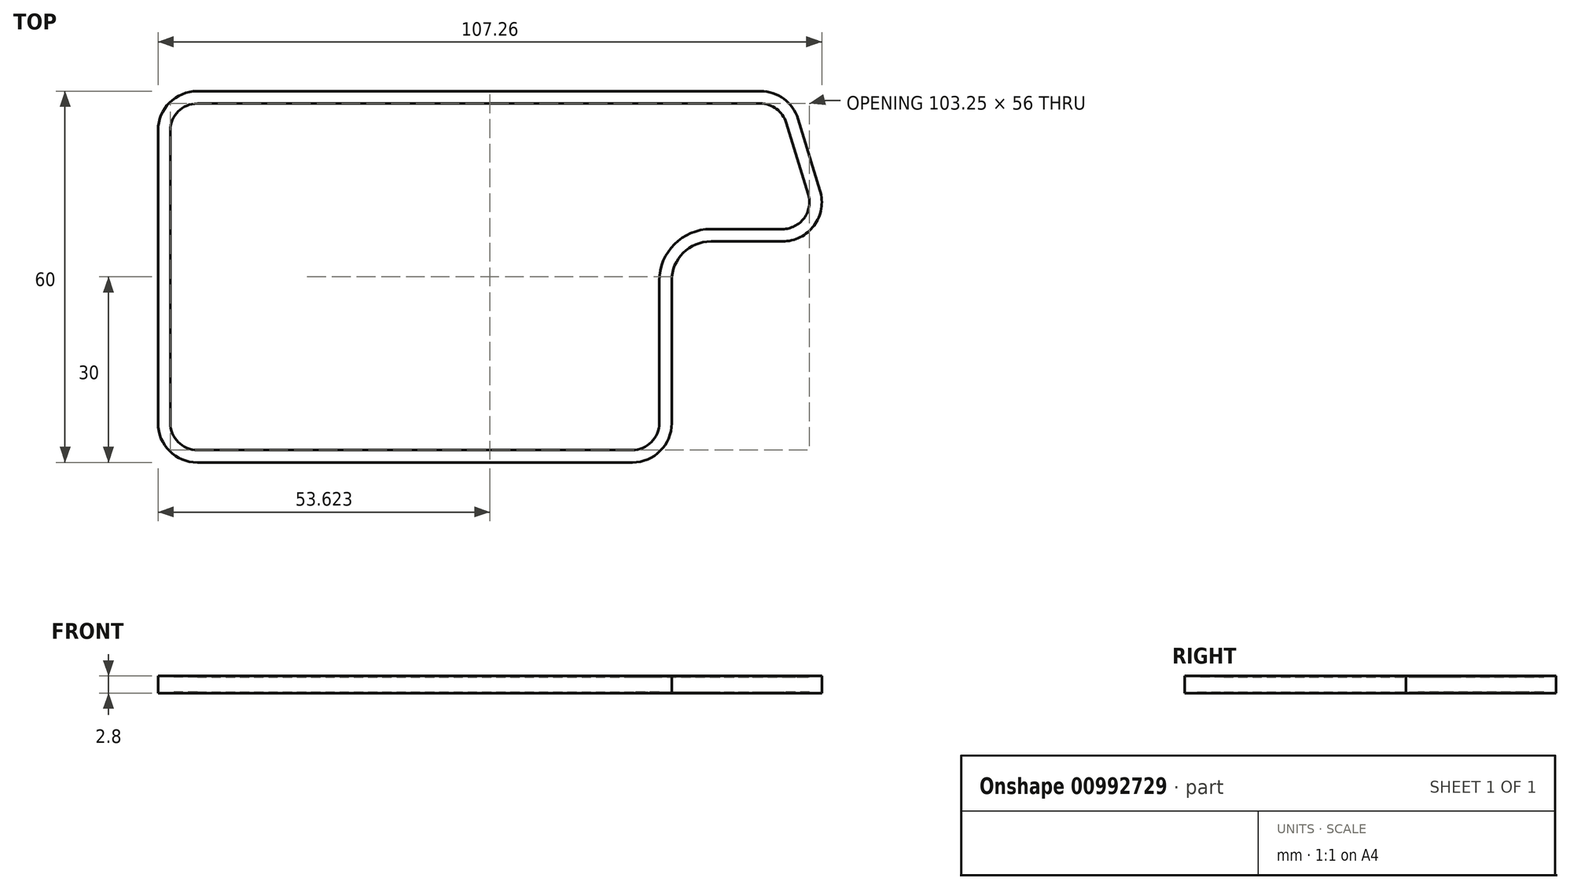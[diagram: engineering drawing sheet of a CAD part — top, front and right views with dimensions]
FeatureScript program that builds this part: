
annotation { "Feature Type Name" : "Feature", "Feature Type Description" : "" }
export const myFeature = defineFeature(function(context is Context, id is Id, definition is map)
    precondition{}
    {
        {
            var Q0;
            Q0=qCreatedBy(makeId("Top.planeOp"),FACE);
            var sketch = newSketch(context, id + "F0", { "sketchPlane" : qUnion([Q0])});
            skLineSegment(sketch, "E0.bottom", {"start": v(-35.15, -30) * mm, "end": v(35.15, -30) * mm});
            skLineSegment(sketch, "E0.top", {"start": v(-35.15, 30) * mm, "end": v(41.5, 30) * mm});
            skLineSegment(sketch, "E0.left", {"start": v(-41.5, -23.65) * mm, "end": v(-41.5, 23.65) * mm});
            skLineSegment(sketch, "E0.right", {"start": v(41.5, -23.65) * mm, "end": v(41.5, -0.64) * mm});
            skPoint(sketch, "E0.middle", {"position": v(0, 0) * mm});
            skPoint(sketch, "E1.visualSharp", {"position": v(-41.5, 30) * mm});
            skArc(sketch, "E1.filletArc", {"start": v(-35.15, 30) * mm, "mid": v(-39.64, 28.14) * mm, "end": v(-41.5, 23.65) * mm});
            skPoint(sketch, "E2.visualSharp", {"position": v(-41.5, -30) * mm});
            skArc(sketch, "E2.filletArc", {"start": v(-41.5, -23.65) * mm, "mid": v(-39.64, -28.14) * mm, "end": v(-35.15, -30) * mm});
            skPoint(sketch, "E3.visualSharp", {"position": v(41.5, -30) * mm});
            skArc(sketch, "E3.filletArc", {"start": v(35.15, -30) * mm, "mid": v(39.64, -28.14) * mm, "end": v(41.5, -23.65) * mm});
            skLineSegment(sketch, "E4.bottom", {"start": v(41.5, 30) * mm, "end": v(55.85, 30) * mm});
            skLineSegment(sketch, "E4.top", {"start": v(47.85, 5.72) * mm, "end": v(59.4, 5.72) * mm});
            skLineSegment(sketch, "E4.right", {"start": v(61.93, 25.51) * mm, "end": v(65.48, 13.93) * mm});
            skPoint(sketch, "E5.visualSharp", {"position": v(60.55, 30) * mm});
            skArc(sketch, "E5.filletArc", {"start": v(61.93, 25.51) * mm, "mid": v(59.63, 28.76) * mm, "end": v(55.85, 30) * mm});
            skPoint(sketch, "E6.visualSharp", {"position": v(68, 5.72) * mm});
            skArc(sketch, "E6.filletArc", {"start": v(59.4, 5.72) * mm, "mid": v(64.51, 8.29) * mm, "end": v(65.48, 13.93) * mm});
            skPoint(sketch, "E7.visualSharp", {"position": v(41.5, 5.72) * mm});
            skArc(sketch, "E7.filletArc", {"start": v(47.85, 5.72) * mm, "mid": v(43.36, 3.86) * mm, "end": v(41.5, -0.64) * mm});
            skSolve(sketch);
        }
        {
            var Q0;
            Q0=makeQuery(id+"F0.imprint","IMPRINT",FACE,{"disambiguationData":[TD([[makeQuery(id+"F0.imprint","IMPRINT",EDGE,{"derivedFrom":sQuery(id+"F0.wireOp",EDGE,"E0.bottom")}),1.0]])]});
            extrude(context, id + "F1", {"entities" : qUnion([Q0]), "depth" : 2.8 * mm, "offsetDistance" : 25.4 * mm});
        }
        {
            var Q0;
            Q0=makeQuery(id+"F1.opExtrude","CAP_FACE",FACE,{"disambiguationData":[OSD([sQuery(id+"F0.wireOp",EDGE,"E0.bottom"),sQuery(id+"F0.wireOp",EDGE,"E0.top"),sQuery(id+"F0.wireOp",EDGE,"E0.left"),sQuery(id+"F0.wireOp",EDGE,"E0.right"),sQuery(id+"F0.wireOp",EDGE,"E1.filletArc"),sQuery(id+"F0.wireOp",EDGE,"E2.filletArc"),sQuery(id+"F0.wireOp",EDGE,"E3.filletArc"),sQuery(id+"F0.wireOp",EDGE,"E4.bottom"),sQuery(id+"F0.wireOp",EDGE,"E4.top"),sQuery(id+"F0.wireOp",EDGE,"E4.right"),sQuery(id+"F0.wireOp",EDGE,"E5.filletArc"),sQuery(id+"F0.wireOp",EDGE,"E6.filletArc"),sQuery(id+"F0.wireOp",EDGE,"E7.filletArc")])],"isStart":false});
            var sketch = newSketch(context, id + "F2", { "sketchPlane" : qUnion([Q0])});
            skLineSegment(sketch, "E8.0", {"start": v(47.85, 7.72) * mm, "end": v(59.4, 7.72) * mm});
            skArc(sketch, "E8.1", {"start": v(-35.15, 28) * mm, "mid": v(-38.23, 26.73) * mm, "end": v(-39.5, 23.65) * mm});
            skLineSegment(sketch, "E8.2", {"start": v(-35.15, 28) * mm, "end": v(55.85, 28) * mm});
            skArc(sketch, "E8.3", {"start": v(60.01, 24.92) * mm, "mid": v(58.44, 27.15) * mm, "end": v(55.85, 28) * mm});
            skLineSegment(sketch, "E8.4", {"start": v(60.01, 24.92) * mm, "end": v(63.56, 13.34) * mm});
            skLineSegment(sketch, "E8.5", {"start": v(-39.5, -23.65) * mm, "end": v(-39.5, 23.65) * mm});
            skArc(sketch, "E8.6", {"start": v(59.4, 7.72) * mm, "mid": v(62.9, 9.48) * mm, "end": v(63.56, 13.34) * mm});
            skArc(sketch, "E8.7", {"start": v(-39.5, -23.65) * mm, "mid": v(-38.23, -26.73) * mm, "end": v(-35.15, -28) * mm});
            skLineSegment(sketch, "E8.8", {"start": v(-35.15, -28) * mm, "end": v(35.15, -28) * mm});
            skArc(sketch, "E8.9", {"start": v(35.15, -28) * mm, "mid": v(38.23, -26.73) * mm, "end": v(39.5, -23.65) * mm});
            skLineSegment(sketch, "E8.10", {"start": v(39.5, -23.65) * mm, "end": v(39.5, -0.63) * mm});
            skArc(sketch, "E8.11", {"start": v(47.85, 7.72) * mm, "mid": v(41.95, 5.27) * mm, "end": v(39.5, -0.63) * mm});
            skSolve(sketch);
        }
        {
            var Q0;
            Q0 = qSketchRegion(id + "F2", true);
            extrude(context, id + "F3", {"entities" : qUnion([Q0]), "operationType" : NewBodyOperationType.REMOVE, "oppositeDirection" : true, "depth" : .2 * mm, "offsetDistance" : 25 * mm});
        }
        {
            var Q0;
            Q0=makeQuery(id+"F1.opExtrude","CAP_FACE",FACE,{"disambiguationData":[OSD([sQuery(id+"F0.wireOp",EDGE,"E0.bottom"),sQuery(id+"F0.wireOp",EDGE,"E0.top"),sQuery(id+"F0.wireOp",EDGE,"E0.left"),sQuery(id+"F0.wireOp",EDGE,"E0.right"),sQuery(id+"F0.wireOp",EDGE,"E1.filletArc"),sQuery(id+"F0.wireOp",EDGE,"E2.filletArc"),sQuery(id+"F0.wireOp",EDGE,"E3.filletArc"),sQuery(id+"F0.wireOp",EDGE,"E4.bottom"),sQuery(id+"F0.wireOp",EDGE,"E4.top"),sQuery(id+"F0.wireOp",EDGE,"E4.right"),sQuery(id+"F0.wireOp",EDGE,"E5.filletArc"),sQuery(id+"F0.wireOp",EDGE,"E6.filletArc"),sQuery(id+"F0.wireOp",EDGE,"E7.filletArc")])],"isStart":true});
            var sketch = newSketch(context, id + "F4", { "sketchPlane" : qUnion([Q0])});
            skLineSegment(sketch, "E9.0", {"start": v(-35.15, -28) * mm, "end": v(55.85, -28) * mm});
            skArc(sketch, "E10.0", {"start": v(-35.15, -28) * mm, "mid": v(-38.23, -26.73) * mm, "end": v(-39.5, -23.65) * mm});
            skLineSegment(sketch, "E11.0", {"start": v(-39.5, 23.65) * mm, "end": v(-39.5, -23.65) * mm});
            skLineSegment(sketch, "E12.0", {"start": v(-35.15, 28) * mm, "end": v(35.15, 28) * mm});
            skArc(sketch, "E13.0", {"start": v(-39.5, 23.65) * mm, "mid": v(-38.23, 26.73) * mm, "end": v(-35.15, 28) * mm});
            skLineSegment(sketch, "E14.0", {"start": v(39.5, 23.65) * mm, "end": v(39.5, 0.63) * mm});
            skArc(sketch, "E15.0", {"start": v(35.15, 28) * mm, "mid": v(38.23, 26.73) * mm, "end": v(39.5, 23.65) * mm});
            skArc(sketch, "E16.0", {"start": v(47.85, -7.72) * mm, "mid": v(41.95, -5.27) * mm, "end": v(39.5, 0.63) * mm});
            skLineSegment(sketch, "E17.0", {"start": v(47.85, -7.72) * mm, "end": v(59.4, -7.72) * mm});
            skArc(sketch, "E18.0", {"start": v(59.4, -7.72) * mm, "mid": v(62.9, -9.48) * mm, "end": v(63.56, -13.34) * mm});
            skLineSegment(sketch, "E19.0", {"start": v(60.01, -24.92) * mm, "end": v(63.56, -13.34) * mm});
            skArc(sketch, "E20.0", {"start": v(60.01, -24.92) * mm, "mid": v(58.44, -27.15) * mm, "end": v(55.85, -28) * mm});
            skSolve(sketch);
        }
        {
            var Q0;
            Q0 = qSketchRegion(id + "F4", true);
            extrude(context, id + "F5", {"entities" : qUnion([Q0]), "operationType" : NewBodyOperationType.REMOVE, "oppositeDirection" : true, "depth" : .2 * mm, "offsetDistance" : 25 * mm});
        }
    });
